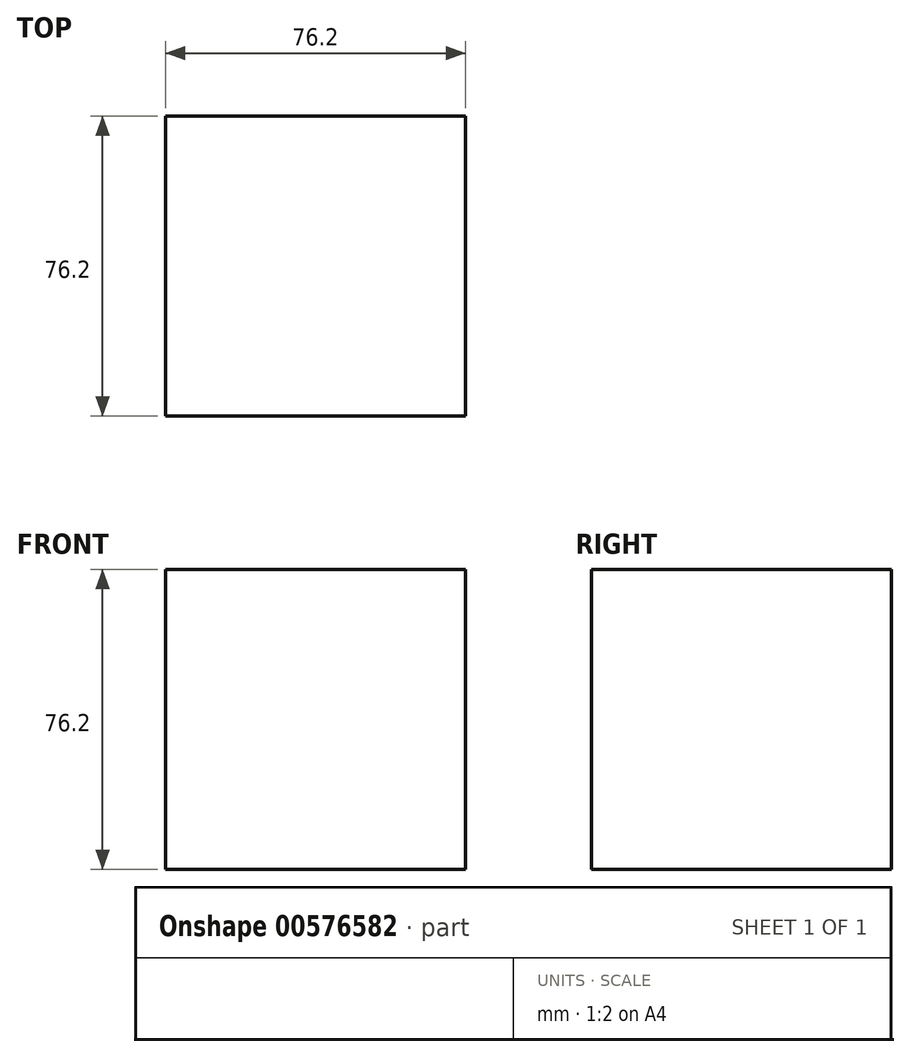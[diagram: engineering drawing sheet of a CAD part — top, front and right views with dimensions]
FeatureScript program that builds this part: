
annotation { "Feature Type Name" : "Feature", "Feature Type Description" : "" }
export const myFeature = defineFeature(function(context is Context, id is Id, definition is map)
    precondition{}
    {
        {
            var Q0;
            Q0=qCreatedBy(makeId("Front.planeOp"),FACE);
            var sketch = newSketch(context, id + "F0", { "sketchPlane" : qUnion([Q0])});
            skLineSegment(sketch, "E0.bottom", {"start": v(0, 0) * mm, "end": v(76.2, 0) * mm});
            skLineSegment(sketch, "E0.top", {"start": v(0, 76.2) * mm, "end": v(76.2, 76.2) * mm});
            skLineSegment(sketch, "E0.left", {"start": v(0, 0) * mm, "end": v(0, 76.2) * mm});
            skLineSegment(sketch, "E0.right", {"start": v(76.2, 0) * mm, "end": v(76.2, 76.2) * mm});
            skSolve(sketch);
        }
        {
            var Q0;
            Q0=makeQuery(id+"F0.imprint","IMPRINT",FACE,{"disambiguationData":[TD([[makeQuery(id+"F0.imprint","IMPRINT",EDGE,{"derivedFrom":sQuery(id+"F0.wireOp",EDGE,"E0.bottom")}),1.0]])]});
            extrude(context, id + "F1", {"entities" : qUnion([Q0]), "depth" : 76.2 * mm, "offsetDistance" : 25.4 * mm});
        }
    });
